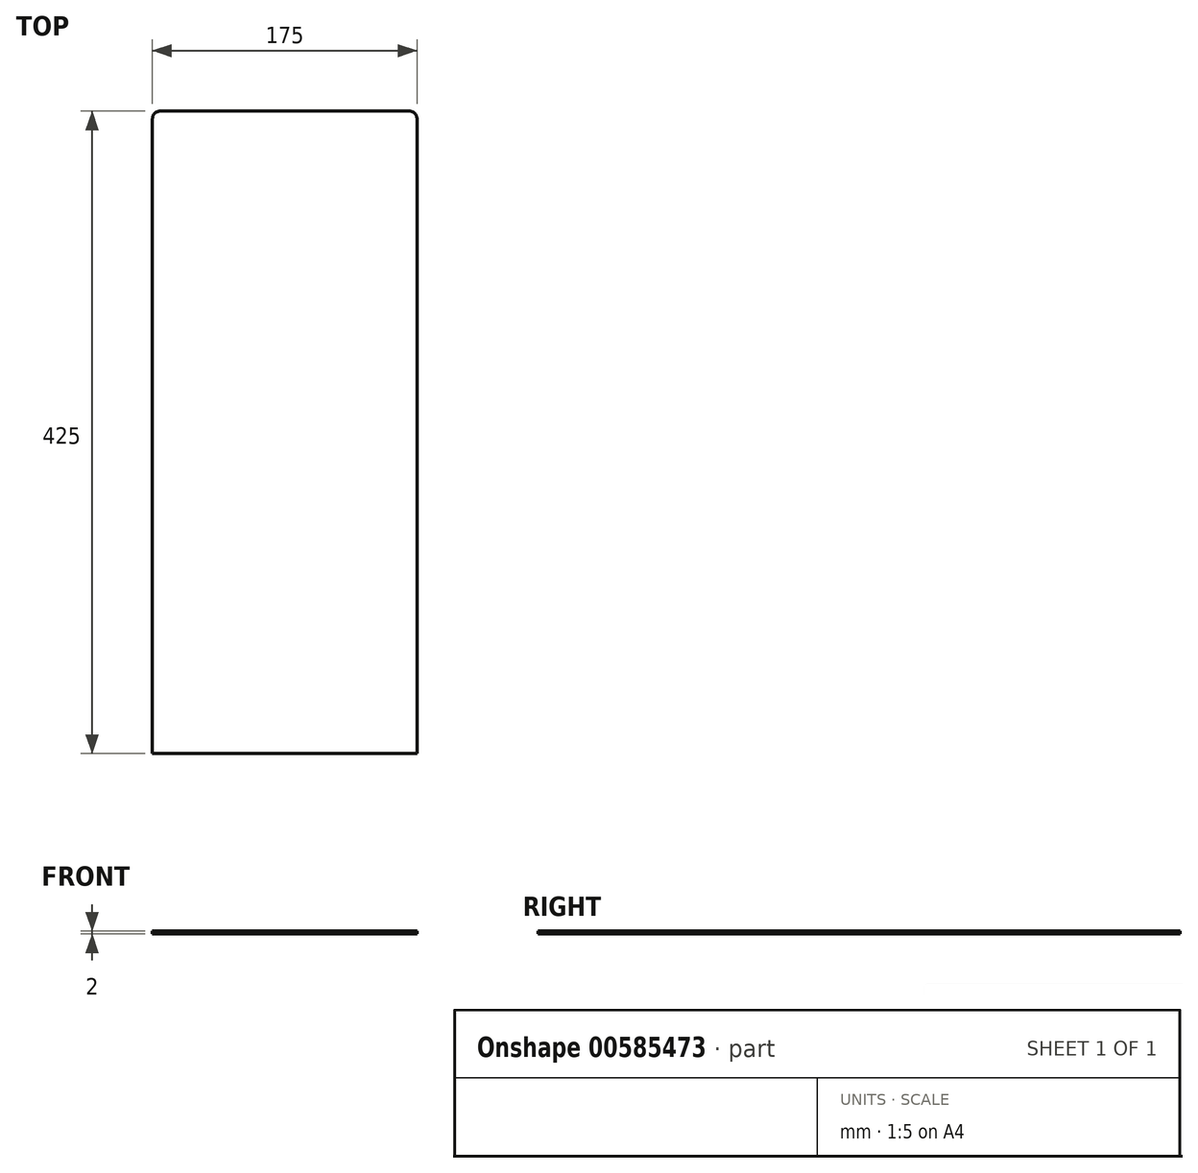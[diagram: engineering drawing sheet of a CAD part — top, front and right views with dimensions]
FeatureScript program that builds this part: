
annotation { "Feature Type Name" : "Feature", "Feature Type Description" : "" }
export const myFeature = defineFeature(function(context is Context, id is Id, definition is map)
    precondition{}
    {
        {
            var Q0;
            Q0=qCreatedBy(makeId("Top.planeOp"),FACE);
            var sketch = newSketch(context, id + "F0", { "sketchPlane" : qUnion([Q0])});
            skLineSegment(sketch, "E0.bottom", {"start": v(87.5, -202.5) * mm, "end": v(-87.5, -202.5) * mm});
            skLineSegment(sketch, "E0.top", {"start": v(87.5, 202.5) * mm, "end": v(-87.5, 202.5) * mm});
            skLineSegment(sketch, "E0.left", {"start": v(87.5, -202.5) * mm, "end": v(87.5, 202.5) * mm});
            skLineSegment(sketch, "E0.right", {"start": v(-87.5, -202.5) * mm, "end": v(-87.5, 202.5) * mm});
            skPoint(sketch, "E0.middle", {"position": v(0, 0) * mm});
            skLineSegment(sketch, "E1", {"start": v(-87.5, 202.5) * mm, "end": v(-87.5, 222.5) * mm});
            skLineSegment(sketch, "E2", {"start": v(-87.5, 222.5) * mm, "end": v(87.5, 222.5) * mm});
            skLineSegment(sketch, "E3", {"start": v(87.5, 222.5) * mm, "end": v(87.5, 202.5) * mm});
            skSolve(sketch);
        }
        {
            var Q0;
            Q0 = qSketchRegion(id + "F0", true);
            extrude(context, id + "F1", {"entities" : qUnion([Q0]), "depth" : 2 * mm, "offsetDistance" : 25 * mm});
        }
        {
            var Q0;
            Q0=makeQuery(id+"F1.opExtrude","SWEPT_EDGE",EDGE,{"disambiguationData":[OSD([sQuery(id+"F0.wireOp",EDGE,"E2"),sQuery(id+"F0.wireOp",EDGE,"E3")])]});
            var Q1;
            Q1=makeQuery(id+"F1.opExtrude","SWEPT_EDGE",EDGE,{"disambiguationData":[OSD([sQuery(id+"F0.wireOp",EDGE,"E1"),sQuery(id+"F0.wireOp",EDGE,"E2")])]});
            fillet(context, id + "F2", {"entities" : qUnion([Q0, Q1]), "radius" : 5 * mm, "tangentPropagation" : true, "allowEdgeOverflow" : false});
        }
    });
